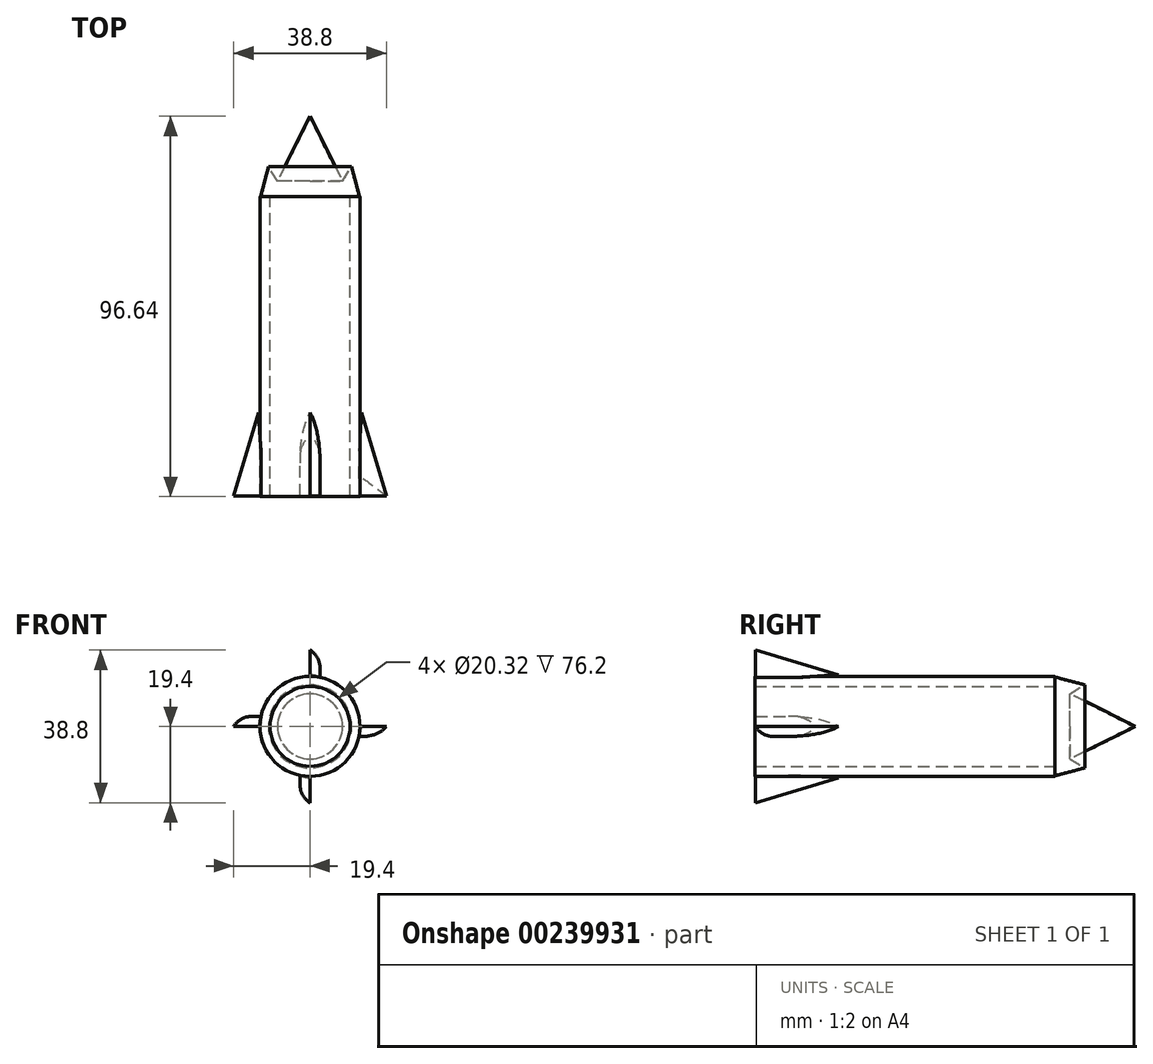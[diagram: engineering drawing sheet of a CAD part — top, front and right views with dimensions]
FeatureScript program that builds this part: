
annotation { "Feature Type Name" : "Feature", "Feature Type Description" : "" }
export const myFeature = defineFeature(function(context is Context, id is Id, definition is map)
    precondition{}
    {
        {
            var Q0;
            Q0=qCreatedBy(makeId("Front.planeOp"),FACE);
            var sketch = newSketch(context, id + "F0", { "sketchPlane" : qUnion([Q0])});
            skCircle(sketch, "E0", {"center": v(0, 0) * mm, "radius": 12.7 * mm});
            skSolve(sketch);
        }
        {
            var Q0;
            Q0=makeQuery(id+"F0.imprint","IMPRINT",FACE,{"disambiguationData":[TD([[makeQuery(id+"F0.imprint","IMPRINT",EDGE,{"derivedFrom":sQuery(id+"F0.wireOp",EDGE,"E0")}),1.0]])]});
            extrude(context, id + "F1", {"entities" : qUnion([Q0]), "depth" : 76.2 * mm});
        }
        {
            var Q0;
            Q0=qCreatedBy(makeId("Front.planeOp"),FACE);
            var sketch = newSketch(context, id + "F2", { "sketchPlane" : qUnion([Q0])});
            skCircle(sketch, "E1", {"center": v(0, 0) * mm, "radius": 10.16 * mm});
            skSolve(sketch);
        }
        {
            var Q0;
            Q0 = qSketchRegion(id + "F2", true);
            extrude(context, id + "F3", {"entities" : qUnion([Q0]), "operationType" : NewBodyOperationType.REMOVE, "depth" : 76.2 * mm});
        }
        {
            var Q0;
            Q0=qCreatedBy(makeId("Top.planeOp"),FACE);
            var sketch = newSketch(context, id + "F4", { "sketchPlane" : qUnion([Q0])});
            skLineSegment(sketch, "E2", {"start": v(-12.55, 0) * mm, "end": v(-10.55, 7.6) * mm});
            skLineSegment(sketch, "E3", {"start": v(-10.55, 7.6) * mm, "end": v(-8.27, 3.9) * mm});
            skLineSegment(sketch, "E4", {"start": v(-8.27, 3.9) * mm, "end": v(0, 20.44) * mm});
            skLineSegment(sketch, "E5", {"start": v(0, 20.44) * mm, "end": v(0, 0) * mm});
            skLineSegment(sketch, "E6", {"start": v(0, 0) * mm, "end": v(-12.55, 0) * mm});
            skSolve(sketch);
        }
        {
            var Q0;
            Q0 = qSketchRegion(id + "F4", true);
            var Q1;
            Q1=sQuery(id+"F4.wireOp",EDGE,"E5");
            revolve(context, id + "F5", {"operationType" : NewBodyOperationType.ADD, "entities" : qUnion([Q0]), "axis" : qUnion([Q1]), "revolveType" : RevolveType.FULL});
        }
        {
            var Q0;
            Q0=qCreatedBy(makeId("Top.planeOp"),FACE);
            var sketch = newSketch(context, id + "F6", { "sketchPlane" : qUnion([Q0])});
            skLineSegment(sketch, "E7", {"start": v(-13.12, -54.9) * mm, "end": v(-19.4, -76.02) * mm});
            skLineSegment(sketch, "E8", {"start": v(-19.4, -76.02) * mm, "end": v(-11.7, -76.02) * mm});
            skLineSegment(sketch, "E9", {"start": v(-11.7, -76.02) * mm, "end": v(-13.12, -54.9) * mm});
            skSolve(sketch);
        }
        {
            var Q0;
            Q0=makeQuery(id+"F6.imprint","IMPRINT",FACE,{"disambiguationData":[TD([[makeQuery(id+"F6.imprint","IMPRINT",EDGE,{"derivedFrom":sQuery(id+"F6.wireOp",EDGE,"E7")}),1.0]])]});
            extrude(context, id + "F7", {"entities" : qUnion([Q0]), "operationType" : NewBodyOperationType.ADD, "depth" : 2.54 * mm});
        }
        {
            var Q0;
            Q0=makeQuery(id+"F1.opExtrude","SWEPT_BODY",BODY,{"disambiguationData":[OSD([sQuery(id+"F0.wireOp",EDGE,"E0")])]});
            var Q1;
            Q1=makeQuery(id+"F3.boolean.opBoolean","COPY",FACE,{"derivedFrom":makeQuery(id+"F3.opExtrude","SWEPT_FACE",FACE,{"disambiguationData":[OSD([sQuery(id+"F2.wireOp",EDGE,"E1")])]})});
            circularPattern(context, id + "F8", {"entities" : qUnion([Q0]), "axis" : qUnion([Q1]), "angle" : 360 * degree, "instanceCount" : 4, "equalSpace" : true});
        }
        {
            var Q0;
            Q0=makeQuery(id+"F8.opPattern","COPY",EDGE,{"derivedFrom":makeQuery(id+"F7.opExtrude","CAP_EDGE",EDGE,{"disambiguationData":[OSD([sQuery(id+"F6.wireOp",EDGE,"E7")])],"isStart":false}),"instanceName":"1"});
            fillet(context, id + "F9", {"entities" : qUnion([Q0]), "radius" : 5.08 * mm, "tangentPropagation" : true, "allowEdgeOverflow" : false});
        }
        {
            var Q0;
            Q0=makeQuery(id+"F8.opPattern","COPY",FACE,{"derivedFrom":makeQuery(id+"F7.opExtrude","SWEPT_FACE",FACE,{"disambiguationData":[OSD([sQuery(id+"F6.wireOp",EDGE,"E8")])]}),"instanceName":"1"});
            var Q1;
            Q1=makeQuery(id+"F8.opPattern","COPY",EDGE,{"derivedFrom":makeQuery(id+"F7.opExtrude","CAP_EDGE",EDGE,{"disambiguationData":[OSD([sQuery(id+"F6.wireOp",EDGE,"E8")])],"isStart":false}),"instanceName":"2"});
            fillet(context, id + "F10", {"entities" : qUnion([Q0, Q1]), "radius" : 5.08 * mm, "tangentPropagation" : true, "allowEdgeOverflow" : false});
        }
        {
            var Q0;
            Q0=makeQuery(id+"F8.opPattern","COPY",EDGE,{"derivedFrom":makeQuery(id+"F7.opExtrude","CAP_EDGE",EDGE,{"disambiguationData":[OSD([sQuery(id+"F6.wireOp",EDGE,"E7")])],"isStart":false}),"instanceName":"2"});
            fillet(context, id + "F11", {"entities" : qUnion([Q0]), "radius" : 5.08 * mm, "tangentPropagation" : true, "allowEdgeOverflow" : false});
        }
        {
            var Q0;
            Q0=makeQuery(id+"F8.opPattern","COPY",EDGE,{"derivedFrom":makeQuery(id+"F7.opExtrude","CAP_EDGE",EDGE,{"disambiguationData":[OSD([sQuery(id+"F6.wireOp",EDGE,"E7")])],"isStart":false}),"instanceName":"3"});
            fillet(context, id + "F12", {"entities" : qUnion([Q0]), "radius" : 5.08 * mm, "tangentPropagation" : true, "allowEdgeOverflow" : false});
        }
        {
            var Q0;
            Q0=makeQuery(id+"F7.opExtrude","CAP_EDGE",EDGE,{"disambiguationData":[OSD([sQuery(id+"F6.wireOp",EDGE,"E7")])],"isStart":false});
            fillet(context, id + "F13", {"entities" : qUnion([Q0]), "radius" : 5.08 * mm, "tangentPropagation" : true, "allowEdgeOverflow" : false});
        }
    });
